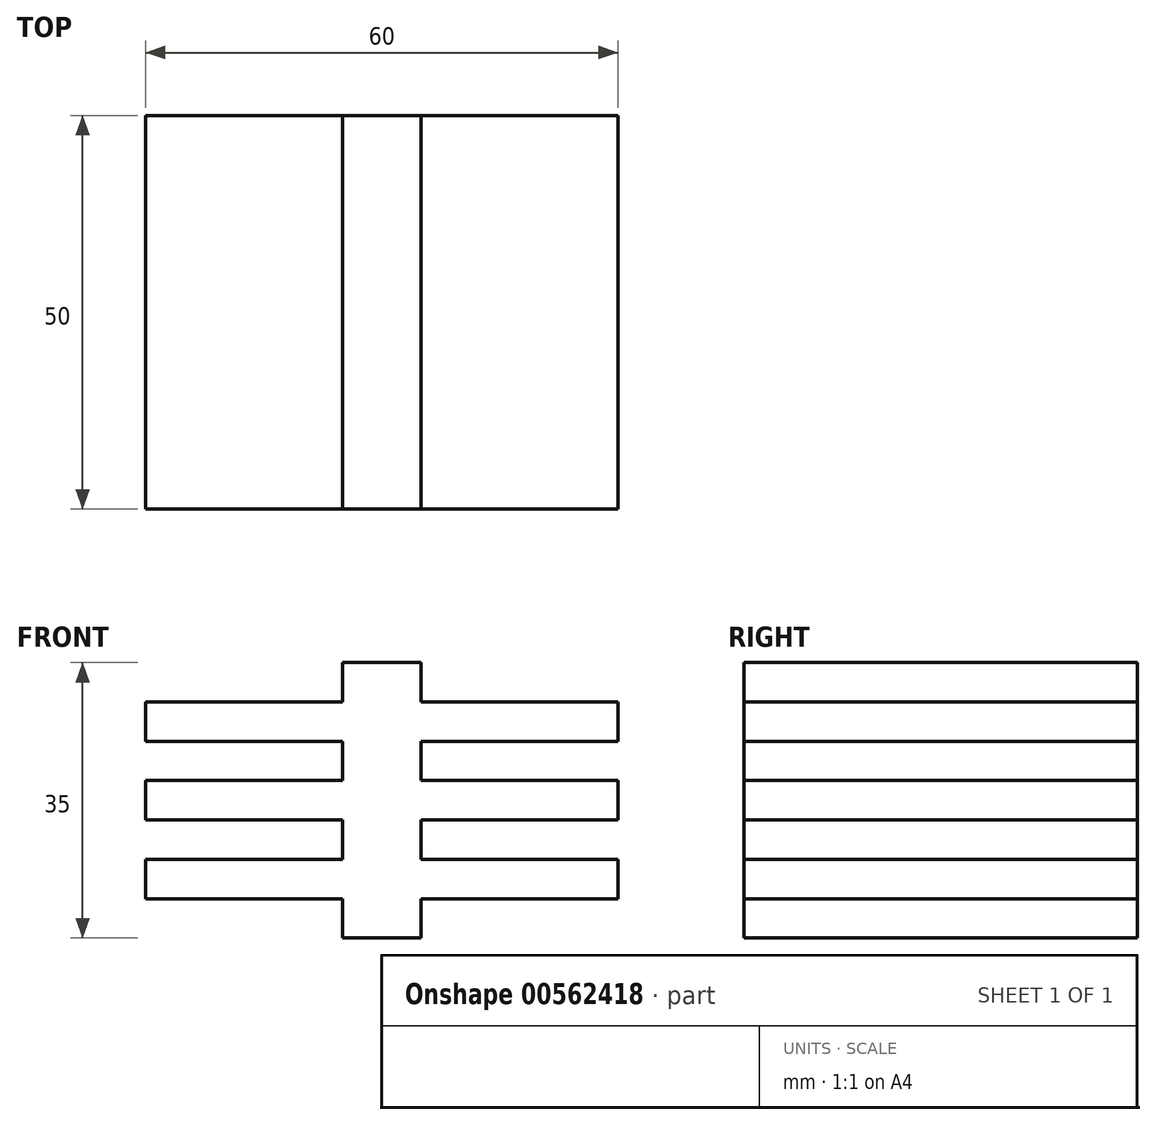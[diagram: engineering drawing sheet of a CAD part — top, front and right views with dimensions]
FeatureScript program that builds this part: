
annotation { "Feature Type Name" : "Feature", "Feature Type Description" : "" }
export const myFeature = defineFeature(function(context is Context, id is Id, definition is map)
    precondition{}
    {
        {
            var Q0;
            Q0=qCreatedBy(makeId("Front.planeOp"),FACE);
            var sketch = newSketch(context, id + "F0", { "sketchPlane" : qUnion([Q0])});
            skLineSegment(sketch, "E0.bottom", {"start": v(-5, 45) * mm, "end": v(5, 45) * mm});
            skLineSegment(sketch, "E0.top", {"start": v(-5, 10) * mm, "end": v(5, 10) * mm});
            skLineSegment(sketch, "E0.left", {"start": v(-5, 45) * mm, "end": v(-5, 10) * mm});
            skLineSegment(sketch, "E0.right", {"start": v(5, 45) * mm, "end": v(5, 10) * mm});
            skLineSegment(sketch, "E1.bottom", {"start": v(-30, 40) * mm, "end": v(30, 40) * mm});
            skLineSegment(sketch, "E1.top", {"start": v(-30, 35) * mm, "end": v(30, 35) * mm});
            skLineSegment(sketch, "E1.left", {"start": v(-30, 40) * mm, "end": v(-30, 35) * mm});
            skLineSegment(sketch, "E1.right", {"start": v(30, 40) * mm, "end": v(30, 35) * mm});
            skLineSegment(sketch, "E2.bottom", {"start": v(-30, 30) * mm, "end": v(30, 30) * mm});
            skLineSegment(sketch, "E2.top", {"start": v(-30, 25) * mm, "end": v(30, 25) * mm});
            skLineSegment(sketch, "E2.left", {"start": v(-30, 30) * mm, "end": v(-30, 25) * mm});
            skLineSegment(sketch, "E2.right", {"start": v(30, 30) * mm, "end": v(30, 25) * mm});
            skLineSegment(sketch, "E3.bottom", {"start": v(-30, 20) * mm, "end": v(30, 20) * mm});
            skLineSegment(sketch, "E3.top", {"start": v(-30, 15) * mm, "end": v(30, 15) * mm});
            skLineSegment(sketch, "E3.left", {"start": v(-30, 20) * mm, "end": v(-30, 15) * mm});
            skLineSegment(sketch, "E3.right", {"start": v(30, 20) * mm, "end": v(30, 15) * mm});
            skSolve(sketch);
        }
        {
            var Q0;
            Q0 = qSketchRegion(id + "F0", true);
            extrude(context, id + "F1", {"entities" : qUnion([Q0]), "depth" : 50 * mm, "offsetDistance" : 25 * mm});
        }
    });
